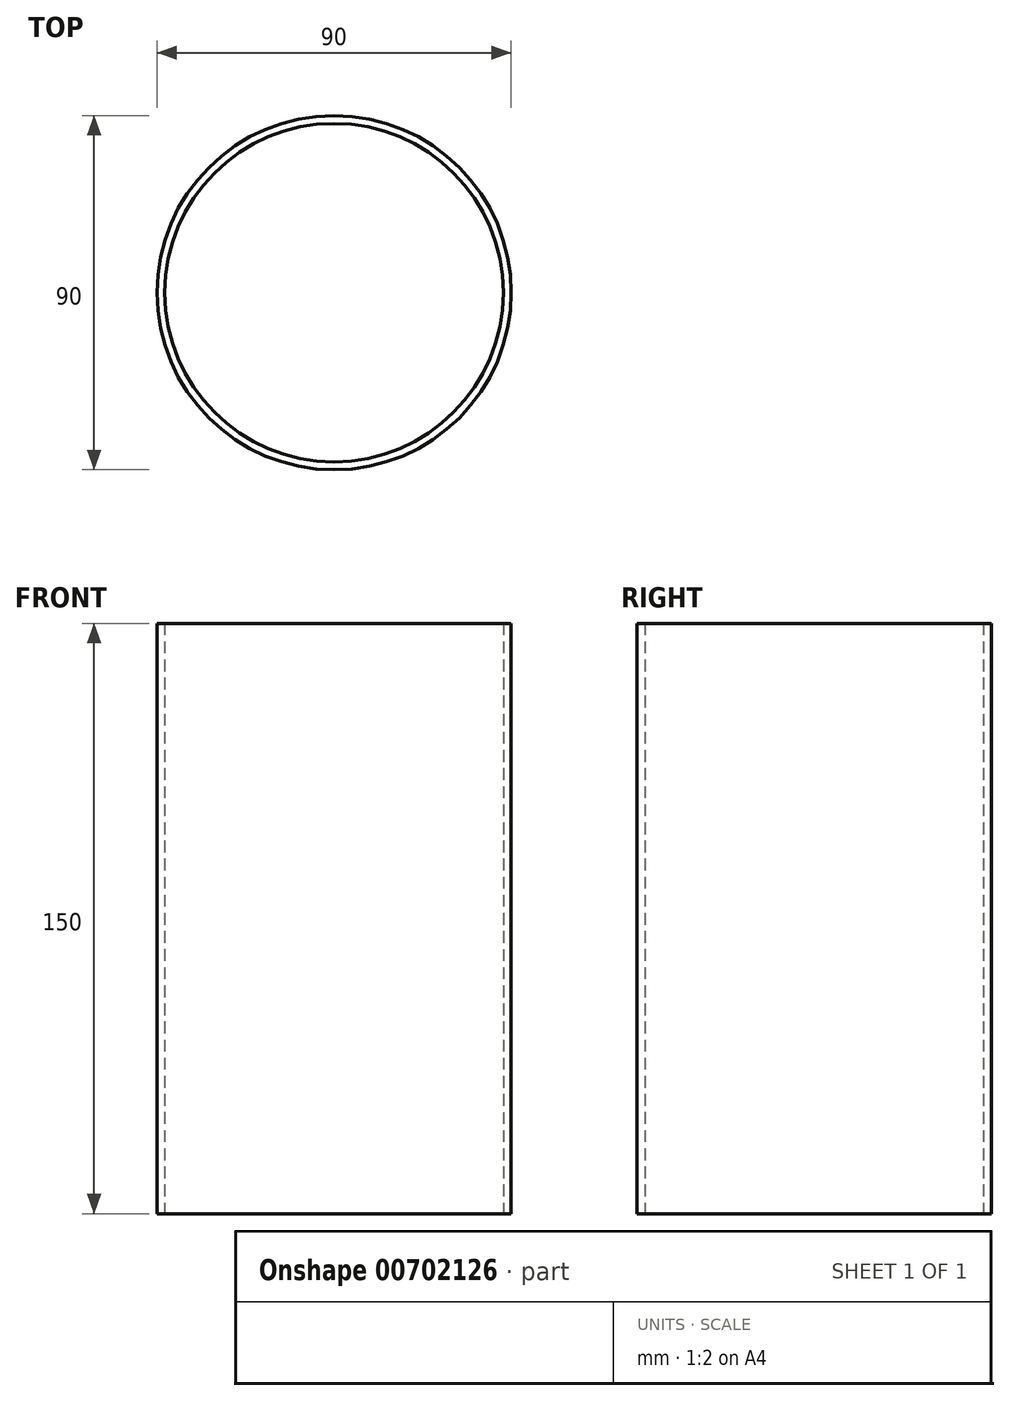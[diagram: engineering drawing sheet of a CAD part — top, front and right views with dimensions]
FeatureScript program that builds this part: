
annotation { "Feature Type Name" : "Feature", "Feature Type Description" : "" }
export const myFeature = defineFeature(function(context is Context, id is Id, definition is map)
    precondition{}
    {
        {
            var Q0;
            Q0=qCreatedBy(makeId("Top.planeOp"),FACE);
            var sketch = newSketch(context, id + "F0", { "sketchPlane" : qUnion([Q0])});
            skCircle(sketch, "E0", {"center": v(0, 0) * mm, "radius": 45 * mm});
            skCircle(sketch, "E1", {"center": v(0, 0) * mm, "radius": 43 * mm});
            skSolve(sketch);
        }
        {
            var Q0;
            Q0=makeQuery(id+"F0.imprint","IMPRINT",FACE,{"disambiguationData":[TD([[makeQuery(id+"F0.imprint","IMPRINT",EDGE,{"derivedFrom":sQuery(id+"F0.wireOp",EDGE,"E0")}),1.0]])]});
            extrude(context, id + "F1", {"entities" : qUnion([Q0]), "depth" : 150 * mm, "offsetDistance" : 25 * mm});
        }
    });
